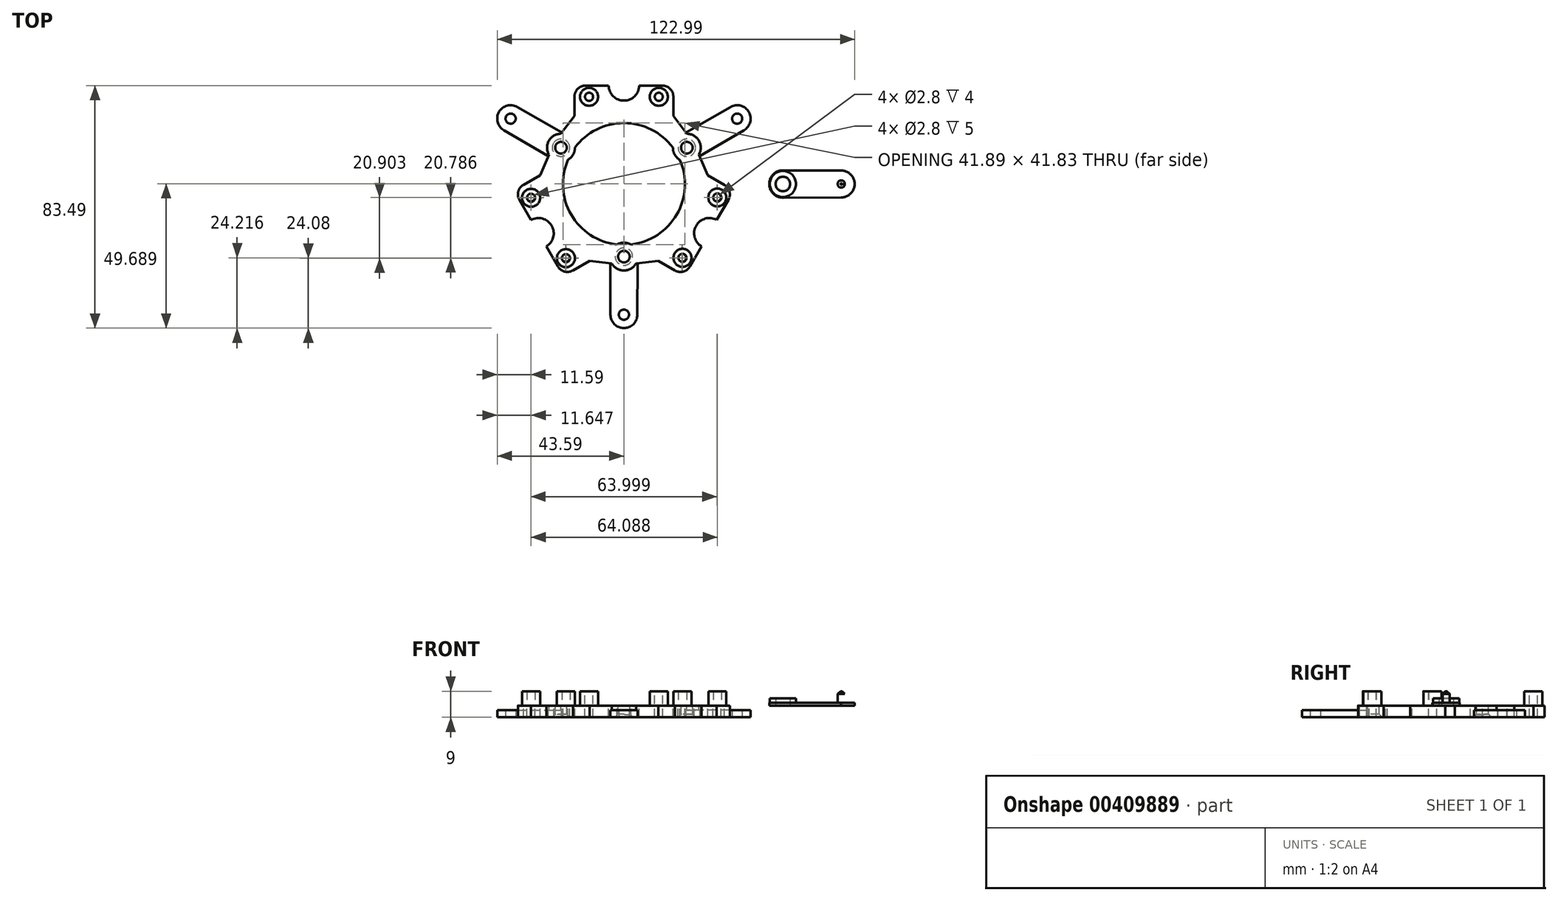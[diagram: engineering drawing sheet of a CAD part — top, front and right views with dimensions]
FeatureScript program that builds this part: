
annotation { "Feature Type Name" : "Feature", "Feature Type Description" : "" }
export const myFeature = defineFeature(function(context is Context, id is Id, definition is map)
    precondition{}
    {
        {
            var Q0;
            Q0=qCreatedBy(makeId("Front.planeOp"),FACE);
            var sketch = newSketch(context, id + "F0", { "sketchPlane" : qUnion([Q0])});
            skLineSegment(sketch, "E0", {"start": v(0, 0) * mm, "end": v(0, 50) * mm});
            skSolve(sketch);
        }
        {
            var Q0;
            Q0=qCreatedBy(makeId("Top.planeOp"),FACE);
            var sketch = newSketch(context, id + "F1", { "sketchPlane" : qUnion([Q0])});
            skCircle(sketch, "E1.cCircle", {"center": v(0, 0) * mm, "radius": 30.02 * mm, "construction": true});
            skLineSegment(sketch, "E1.0", {"start": v(-52, 30.02) * mm, "end": v(52, 30.02) * mm});
            skLineSegment(sketch, "E1.1", {"start": v(52, 30.02) * mm, "end": v(0, -60.04) * mm});
            skLineSegment(sketch, "E1.2", {"start": v(0, -60.04) * mm, "end": v(-52, 30.02) * mm});
            skPoint(sketch, "E1.0.midPoint", {"position": v(0, 30.02) * mm});
            skCircle(sketch, "E2", {"center": v(12, 30.02) * mm, "radius": 1.25 * mm});
            skCircle(sketch, "E3.MirrorC", {"center": v(-12, 30.02) * mm, "radius": 1.25 * mm});
            skCircle(sketch, "E4.1.0", {"center": v(-32, -4.62) * mm, "radius": 1.25 * mm});
            skCircle(sketch, "E4.1.1", {"center": v(-20, -25.4) * mm, "radius": 1.25 * mm});
            skCircle(sketch, "E4.2.0", {"center": v(20, -25.4) * mm, "radius": 1.25 * mm});
            skCircle(sketch, "E4.2.1", {"center": v(32, -4.62) * mm, "radius": 1.25 * mm});
            skSolve(sketch);
        }
        {
            var Q0;
            Q0=qCreatedBy(makeId("Top.planeOp"),FACE);
            var sketch = newSketch(context, id + "F2", { "sketchPlane" : qUnion([Q0])});
            skLineSegment(sketch, "E5", {"start": v(5.25, 33.87) * mm, "end": v(10.75, 33.87) * mm});
            skArc(sketch, "E6", {"start": v(16.85, 12.5) * mm, "mid": v(9.43, 18.74) * mm, "end": v(0, 20.98) * mm});
            skArc(sketch, "E7", {"start": v(0, 28.71) * mm, "mid": v(3.68, 30.22) * mm, "end": v(5.25, 33.87) * mm});
            skLineSegment(sketch, "E8", {"start": v(10.75, 33.87) * mm, "end": v(13.25, 33.87) * mm});
            skLineSegment(sketch, "E9", {"start": v(12, 33.87) * mm, "end": v(12, 30.02) * mm});
            skCircle(sketch, "E10", {"center": v(21.65, 12.5) * mm, "radius": 2 * mm});
            skArc(sketch, "E11", {"start": v(16.85, 12.5) * mm, "mid": v(25.04, 9.1) * mm, "end": v(21.65, 17.3) * mm});
            skArc(sketch, "E12", {"start": v(17, 30.02) * mm, "mid": v(15.94, 32.74) * mm, "end": v(13.25, 33.87) * mm});
            skLineSegment(sketch, "E13", {"start": v(17, 30.02) * mm, "end": v(17, 23.47) * mm});
            skLineSegment(sketch, "E14", {"start": v(17, 23.47) * mm, "end": v(21.65, 17.3) * mm});
            skLineSegment(sketch, "E15.MirrorCS", {"start": v(-10.75, 33.87) * mm, "end": v(-13.25, 33.87) * mm});
            skLineSegment(sketch, "E16.MirrorCS", {"start": v(-12, 33.87) * mm, "end": v(-12, 30.02) * mm});
            skLineSegment(sketch, "E17.MirrorCS", {"start": v(-17, 23.47) * mm, "end": v(-21.65, 17.3) * mm});
            skArc(sketch, "E18.MirrorCS", {"start": v(-16.85, 12.5) * mm, "mid": v(-25.04, 9.1) * mm, "end": v(-21.65, 17.3) * mm});
            skLineSegment(sketch, "E19.MirrorCS", {"start": v(-5.25, 33.87) * mm, "end": v(-10.75, 33.87) * mm});
            skLineSegment(sketch, "E20.MirrorCS", {"start": v(-17, 30.02) * mm, "end": v(-17, 23.47) * mm});
            skArc(sketch, "E21.MirrorCS", {"start": v(-17, 30.02) * mm, "mid": v(-15.94, 32.74) * mm, "end": v(-13.25, 33.87) * mm});
            skCircle(sketch, "E22.MirrorC", {"center": v(-21.65, 12.5) * mm, "radius": 2 * mm});
            skArc(sketch, "E23.MirrorCS", {"start": v(0, 28.71) * mm, "mid": v(-3.68, 30.22) * mm, "end": v(-5.25, 33.87) * mm});
            skArc(sketch, "E24.MirrorCS", {"start": v(-16.85, 12.5) * mm, "mid": v(-9.43, 18.74) * mm, "end": v(0, 20.98) * mm});
            skArc(sketch, "E25.1.0", {"start": v(-24.87, -14.36) * mm, "mid": v(-28, -11.92) * mm, "end": v(-31.96, -12.39) * mm});
            skLineSegment(sketch, "E25.1.1", {"start": v(-23.33, -27.33) * mm, "end": v(-20, -25.4) * mm});
            skArc(sketch, "E25.1.2", {"start": v(-19.25, 8.34) * mm, "mid": v(-20.4, 17.14) * mm, "end": v(-25.8, 10.1) * mm});
            skLineSegment(sketch, "E25.1.4", {"start": v(-31.96, -12.39) * mm, "end": v(-34.7, -7.63) * mm});
            skLineSegment(sketch, "E25.1.5", {"start": v(-35.33, -6.54) * mm, "end": v(-32, -4.62) * mm});
            skArc(sketch, "E25.1.6", {"start": v(-19.25, 8.34) * mm, "mid": v(-20.95, -1.2) * mm, "end": v(-18.17, -10.5) * mm});
            skArc(sketch, "E25.1.7", {"start": v(-34.5, -0.29) * mm, "mid": v(-36.32, -2.57) * mm, "end": v(-35.96, -5.46) * mm});
            skArc(sketch, "E25.1.8", {"start": v(-24.87, -14.36) * mm, "mid": v(-24.33, -18.3) * mm, "end": v(-26.7, -21.48) * mm});
            skCircle(sketch, "E25.1.9", {"center": v(0, -25) * mm, "radius": 2 * mm});
            skLineSegment(sketch, "E25.1.10", {"start": v(-28.83, 2.99) * mm, "end": v(-25.8, 10.1) * mm});
            skArc(sketch, "E25.1.11", {"start": v(-2.4, -20.84) * mm, "mid": v(-11.51, -17.54) * mm, "end": v(-18.17, -10.5) * mm});
            skArc(sketch, "E25.1.12", {"start": v(-17.5, -29.73) * mm, "mid": v(-20.38, -30.17) * mm, "end": v(-22.7, -28.41) * mm});
            skLineSegment(sketch, "E25.1.13", {"start": v(-34.5, -0.29) * mm, "end": v(-28.83, 2.99) * mm});
            skArc(sketch, "E25.1.14", {"start": v(-2.4, -20.84) * mm, "mid": v(4.64, -26.24) * mm, "end": v(-4.16, -27.4) * mm});
            skLineSegment(sketch, "E25.1.15", {"start": v(-26.7, -21.48) * mm, "end": v(-23.96, -26.24) * mm});
            skLineSegment(sketch, "E25.1.16", {"start": v(-11.83, -26.46) * mm, "end": v(-4.16, -27.4) * mm});
            skLineSegment(sketch, "E25.1.17", {"start": v(-17.5, -29.73) * mm, "end": v(-11.83, -26.46) * mm});
            skLineSegment(sketch, "E25.1.18", {"start": v(-34.7, -7.63) * mm, "end": v(-35.96, -5.46) * mm});
            skLineSegment(sketch, "E25.1.19", {"start": v(-23.96, -26.24) * mm, "end": v(-22.7, -28.41) * mm});
            skArc(sketch, "E25.2.0", {"start": v(24.87, -14.36) * mm, "mid": v(24.33, -18.3) * mm, "end": v(26.7, -21.48) * mm});
            skLineSegment(sketch, "E25.2.1", {"start": v(35.33, -6.54) * mm, "end": v(32, -4.62) * mm});
            skArc(sketch, "E25.2.2", {"start": v(2.4, -20.84) * mm, "mid": v(-4.64, -26.24) * mm, "end": v(4.16, -27.4) * mm});
            skCircle(sketch, "E25.2.3", {"center": v(0, -25) * mm, "radius": 2 * mm});
            skLineSegment(sketch, "E25.2.4", {"start": v(26.7, -21.48) * mm, "end": v(23.96, -26.24) * mm});
            skLineSegment(sketch, "E25.2.5", {"start": v(23.33, -27.33) * mm, "end": v(20, -25.4) * mm});
            skArc(sketch, "E25.2.6", {"start": v(2.4, -20.84) * mm, "mid": v(11.51, -17.54) * mm, "end": v(18.17, -10.5) * mm});
            skArc(sketch, "E25.2.7", {"start": v(17.5, -29.73) * mm, "mid": v(20.38, -30.17) * mm, "end": v(22.7, -28.41) * mm});
            skArc(sketch, "E25.2.8", {"start": v(24.87, -14.36) * mm, "mid": v(28, -11.92) * mm, "end": v(31.96, -12.39) * mm});
            skLineSegment(sketch, "E25.2.10", {"start": v(11.83, -26.46) * mm, "end": v(4.16, -27.4) * mm});
            skArc(sketch, "E25.2.11", {"start": v(19.25, 8.34) * mm, "mid": v(20.95, -1.2) * mm, "end": v(18.17, -10.5) * mm});
            skArc(sketch, "E25.2.12", {"start": v(34.5, -0.29) * mm, "mid": v(36.32, -2.57) * mm, "end": v(35.96, -5.46) * mm});
            skLineSegment(sketch, "E25.2.13", {"start": v(17.5, -29.73) * mm, "end": v(11.83, -26.46) * mm});
            skArc(sketch, "E25.2.14", {"start": v(19.25, 8.34) * mm, "mid": v(20.4, 17.14) * mm, "end": v(25.8, 10.1) * mm});
            skLineSegment(sketch, "E25.2.15", {"start": v(31.96, -12.39) * mm, "end": v(34.7, -7.63) * mm});
            skLineSegment(sketch, "E25.2.16", {"start": v(28.83, 2.99) * mm, "end": v(25.8, 10.1) * mm});
            skLineSegment(sketch, "E25.2.17", {"start": v(34.5, -0.29) * mm, "end": v(28.83, 2.99) * mm});
            skLineSegment(sketch, "E25.2.18", {"start": v(23.96, -26.24) * mm, "end": v(22.7, -28.41) * mm});
            skLineSegment(sketch, "E25.2.19", {"start": v(34.7, -7.63) * mm, "end": v(35.96, -5.46) * mm});
            skCircle(sketch, "E26", {"center": v(12, 30.02) * mm, "radius": 1.4 * mm});
            skCircle(sketch, "E27.MirrorC", {"center": v(-12, 30.02) * mm, "radius": 1.4 * mm});
            skCircle(sketch, "E28.1.0", {"center": v(-32, -4.62) * mm, "radius": 1.4 * mm});
            skCircle(sketch, "E28.1.1", {"center": v(-20, -25.4) * mm, "radius": 1.4 * mm});
            skCircle(sketch, "E28.2.0", {"center": v(20, -25.4) * mm, "radius": 1.4 * mm});
            skCircle(sketch, "E28.2.1", {"center": v(32, -4.62) * mm, "radius": 1.4 * mm});
            skSolve(sketch);
        }
        {
            var Q0;
            Q0=qSketchRegion(id+"F2",true);
            extrude(context, id + "F3", {"entities" : qUnion([Q0]), "oppositeDirection" : true, "depth" : 4 * mm});
        }
        {
            var Q0;
            Q0=makeQuery(id+"F3.opExtrude","CAP_FACE",FACE,{"disambiguationData":[OSD([sQuery(id+"F2.wireOp",EDGE,"E5"),sQuery(id+"F2.wireOp",EDGE,"E6"),sQuery(id+"F2.wireOp",EDGE,"OTH0FymN-yfsN-0UsN-41Kz-5CJosObtJ083"),sQuery(id+"F2.wireOp",EDGE,"3A02pTdK-AV8J-qCXS-i5Cg-76qnhJVGPjWh"),sQuery(id+"F2.wireOp",EDGE,"5Z3o6wOb-oYhe-xRQF-fwUz-g2kkQ9HctwZJ"),sQuery(id+"F2.wireOp",EDGE,"E7"),sQuery(id+"F2.wireOp",EDGE,"AUobkKVc-RQ03-aKL8-U0OO-zYTzcYtjvFHw"),sQuery(id+"F2.wireOp",EDGE,"E8"),sQuery(id+"F2.wireOp",EDGE,"624812f1-2ad6-4ab7-8a89-68286fdeb31e8.MirrorCS"),sQuery(id+"F2.wireOp",EDGE,"624812f1-2ad6-4ab7-8a89-68286fdeb31e9.MirrorCS"),sQuery(id+"F2.wireOp",EDGE,"624812f1-2ad6-4ab7-8a89-68286fdeb31e10.MirrorCS"),sQuery(id+"F2.wireOp",EDGE,"624812f1-2ad6-4ab7-8a89-68286fdeb31e11.MirrorCS"),sQuery(id+"F2.wireOp",EDGE,"624812f1-2ad6-4ab7-8a89-68286fdeb31e12.MirrorCS"),sQuery(id+"F2.wireOp",EDGE,"624812f1-2ad6-4ab7-8a89-68286fdeb31e14.MirrorCS"),sQuery(id+"F2.wireOp",EDGE,"624812f1-2ad6-4ab7-8a89-68286fdeb31e15.MirrorCS"),sQuery(id+"F2.wireOp",EDGE,"624812f1-2ad6-4ab7-8a89-68286fdeb31e16.MirrorCS"),sQuery(id+"F2.wireOp",EDGE,"36ff6b61-fbfb-4fdb-958a-ac3ee2e7cda7.1.1"),sQuery(id+"F2.wireOp",EDGE,"36ff6b61-fbfb-4fdb-958a-ac3ee2e7cda7.1.2"),sQuery(id+"F2.wireOp",EDGE,"36ff6b61-fbfb-4fdb-958a-ac3ee2e7cda7.1.3"),sQuery(id+"F2.wireOp",EDGE,"36ff6b61-fbfb-4fdb-958a-ac3ee2e7cda7.1.4"),sQuery(id+"F2.wireOp",EDGE,"36ff6b61-fbfb-4fdb-958a-ac3ee2e7cda7.1.5"),sQuery(id+"F2.wireOp",EDGE,"36ff6b61-fbfb-4fdb-958a-ac3ee2e7cda7.1.6"),sQuery(id+"F2.wireOp",EDGE,"36ff6b61-fbfb-4fdb-958a-ac3ee2e7cda7.1.7"),sQuery(id+"F2.wireOp",EDGE,"36ff6b61-fbfb-4fdb-958a-ac3ee2e7cda7.1.8"),sQuery(id+"F2.wireOp",EDGE,"36ff6b61-fbfb-4fdb-958a-ac3ee2e7cda7.1.9"),sQuery(id+"F2.wireOp",EDGE,"36ff6b61-fbfb-4fdb-958a-ac3ee2e7cda7.1.10"),sQuery(id+"F2.wireOp",EDGE,"36ff6b61-fbfb-4fdb-958a-ac3ee2e7cda7.1.11"),sQuery(id+"F2.wireOp",EDGE,"36ff6b61-fbfb-4fdb-958a-ac3ee2e7cda7.1.12"),sQuery(id+"F2.wireOp",EDGE,"36ff6b61-fbfb-4fdb-958a-ac3ee2e7cda7.1.15"),sQuery(id+"F2.wireOp",EDGE,"36ff6b61-fbfb-4fdb-958a-ac3ee2e7cda7.1.16"),sQuery(id+"F2.wireOp",EDGE,"36ff6b61-fbfb-4fdb-958a-ac3ee2e7cda7.1.17"),sQuery(id+"F2.wireOp",EDGE,"36ff6b61-fbfb-4fdb-958a-ac3ee2e7cda7.1.19"),sQuery(id+"F2.wireOp",EDGE,"36ff6b61-fbfb-4fdb-958a-ac3ee2e7cda7.2.1"),sQuery(id+"F2.wireOp",EDGE,"36ff6b61-fbfb-4fdb-958a-ac3ee2e7cda7.2.2"),sQuery(id+"F2.wireOp",EDGE,"36ff6b61-fbfb-4fdb-958a-ac3ee2e7cda7.2.3"),sQuery(id+"F2.wireOp",EDGE,"36ff6b61-fbfb-4fdb-958a-ac3ee2e7cda7.2.4"),sQuery(id+"F2.wireOp",EDGE,"36ff6b61-fbfb-4fdb-958a-ac3ee2e7cda7.2.5"),sQuery(id+"F2.wireOp",EDGE,"36ff6b61-fbfb-4fdb-958a-ac3ee2e7cda7.2.6"),sQuery(id+"F2.wireOp",EDGE,"36ff6b61-fbfb-4fdb-958a-ac3ee2e7cda7.2.7"),sQuery(id+"F2.wireOp",EDGE,"36ff6b61-fbfb-4fdb-958a-ac3ee2e7cda7.2.8"),sQuery(id+"F2.wireOp",EDGE,"36ff6b61-fbfb-4fdb-958a-ac3ee2e7cda7.2.9"),sQuery(id+"F2.wireOp",EDGE,"36ff6b61-fbfb-4fdb-958a-ac3ee2e7cda7.2.10"),sQuery(id+"F2.wireOp",EDGE,"36ff6b61-fbfb-4fdb-958a-ac3ee2e7cda7.2.11"),sQuery(id+"F2.wireOp",EDGE,"36ff6b61-fbfb-4fdb-958a-ac3ee2e7cda7.2.12"),sQuery(id+"F2.wireOp",EDGE,"36ff6b61-fbfb-4fdb-958a-ac3ee2e7cda7.2.15"),sQuery(id+"F2.wireOp",EDGE,"36ff6b61-fbfb-4fdb-958a-ac3ee2e7cda7.2.16"),sQuery(id+"F2.wireOp",EDGE,"36ff6b61-fbfb-4fdb-958a-ac3ee2e7cda7.2.17"),sQuery(id+"F2.wireOp",EDGE,"36ff6b61-fbfb-4fdb-958a-ac3ee2e7cda7.2.19")])],"isStart":true});
            var sketch = newSketch(context, id + "F4", { "sketchPlane" : qUnion([Q0])});
            skCircle(sketch, "E29", {"center": v(12, 30.02) * mm, "radius": 1.4 * mm});
            skCircle(sketch, "E30", {"center": v(12, 30.02) * mm, "radius": 3.1 * mm});
            skCircle(sketch, "E31.MirrorC", {"center": v(-12, 30.02) * mm, "radius": 1.4 * mm});
            skCircle(sketch, "E32.MirrorC", {"center": v(-12, 30.02) * mm, "radius": 3.1 * mm});
            skCircle(sketch, "E33.1.0", {"center": v(-19.94, -25.54) * mm, "radius": 3.1 * mm});
            skCircle(sketch, "E33.1.1", {"center": v(-31.94, -4.75) * mm, "radius": 3.1 * mm});
            skCircle(sketch, "E33.1.2", {"center": v(-19.94, -25.54) * mm, "radius": 1.4 * mm});
            skCircle(sketch, "E33.1.3", {"center": v(-31.94, -4.75) * mm, "radius": 1.4 * mm});
            skCircle(sketch, "E33.2.0", {"center": v(32.15, -4.64) * mm, "radius": 3.1 * mm});
            skCircle(sketch, "E33.2.1", {"center": v(20.15, -25.42) * mm, "radius": 3.1 * mm});
            skCircle(sketch, "E33.2.2", {"center": v(32.15, -4.64) * mm, "radius": 1.4 * mm});
            skCircle(sketch, "E33.2.3", {"center": v(20.15, -25.42) * mm, "radius": 1.4 * mm});
            skPoint(sketch, "E33.center", {"position": v(0.07, -0.05) * mm});
            skSolve(sketch);
        }
        {
            var Q0;
            Q0=qSketchRegion(id+"F4",true);
            extrude(context, id + "F5", {"entities" : qUnion([Q0]), "operationType" : NewBodyOperationType.ADD, "depth" : 5 * mm});
        }
        {
            var Q0;
            Q0=qCreatedBy(makeId("Top.planeOp"),FACE);
            cPlane(context, id + "F6", {"entities" : qUnion([Q0]), "cplaneType" : CPlaneType.OFFSET, "offset" : 2 * mm, "oppositeDirection" : true, "width" : 150 * mm, "height" : 150 * mm});
        }
        {
            var Q0;
            Q0=makeQuery(id+"F3.opExtrude","CAP_FACE",FACE,{"disambiguationData":[OSD([sQuery(id+"F2.wireOp",EDGE,"E5"),sQuery(id+"F2.wireOp",EDGE,"E6"),sQuery(id+"F2.wireOp",EDGE,"E7"),sQuery(id+"F2.wireOp",EDGE,"E8"),sQuery(id+"F2.wireOp",EDGE,"E10"),sQuery(id+"F2.wireOp",EDGE,"E11"),sQuery(id+"F2.wireOp",EDGE,"E12"),sQuery(id+"F2.wireOp",EDGE,"E13"),sQuery(id+"F2.wireOp",EDGE,"E14"),sQuery(id+"F2.wireOp",EDGE,"E15.MirrorCS"),sQuery(id+"F2.wireOp",EDGE,"E17.MirrorCS"),sQuery(id+"F2.wireOp",EDGE,"E18.MirrorCS"),sQuery(id+"F2.wireOp",EDGE,"E19.MirrorCS"),sQuery(id+"F2.wireOp",EDGE,"E20.MirrorCS"),sQuery(id+"F2.wireOp",EDGE,"E21.MirrorCS"),sQuery(id+"F2.wireOp",EDGE,"E22.MirrorC"),sQuery(id+"F2.wireOp",EDGE,"E23.MirrorCS"),sQuery(id+"F2.wireOp",EDGE,"E24.MirrorCS"),sQuery(id+"F2.wireOp",EDGE,"E25.1.0"),sQuery(id+"F2.wireOp",EDGE,"E25.1.2"),sQuery(id+"F2.wireOp",EDGE,"E22.MirrorC"),sQuery(id+"F2.wireOp",EDGE,"E25.1.4"),sQuery(id+"F2.wireOp",EDGE,"E25.1.6"),sQuery(id+"F2.wireOp",EDGE,"E25.1.7"),sQuery(id+"F2.wireOp",EDGE,"E25.1.8"),sQuery(id+"F2.wireOp",EDGE,"E25.1.9"),sQuery(id+"F2.wireOp",EDGE,"E25.1.10"),sQuery(id+"F2.wireOp",EDGE,"E25.1.11"),sQuery(id+"F2.wireOp",EDGE,"E25.1.12"),sQuery(id+"F2.wireOp",EDGE,"E25.1.13"),sQuery(id+"F2.wireOp",EDGE,"E25.1.14"),sQuery(id+"F2.wireOp",EDGE,"E25.1.15"),sQuery(id+"F2.wireOp",EDGE,"E25.1.16"),sQuery(id+"F2.wireOp",EDGE,"E25.1.17"),sQuery(id+"F2.wireOp",EDGE,"E25.1.18"),sQuery(id+"F2.wireOp",EDGE,"E25.1.19"),sQuery(id+"F2.wireOp",EDGE,"E25.2.0"),sQuery(id+"F2.wireOp",EDGE,"E25.2.2"),sQuery(id+"F2.wireOp",EDGE,"E25.2.3"),sQuery(id+"F2.wireOp",EDGE,"E25.2.4"),sQuery(id+"F2.wireOp",EDGE,"E25.2.6"),sQuery(id+"F2.wireOp",EDGE,"E25.2.7"),sQuery(id+"F2.wireOp",EDGE,"E25.2.8"),sQuery(id+"F2.wireOp",EDGE,"E10"),sQuery(id+"F2.wireOp",EDGE,"E25.2.10"),sQuery(id+"F2.wireOp",EDGE,"E25.2.11"),sQuery(id+"F2.wireOp",EDGE,"E25.2.12"),sQuery(id+"F2.wireOp",EDGE,"E25.2.13"),sQuery(id+"F2.wireOp",EDGE,"E25.2.14"),sQuery(id+"F2.wireOp",EDGE,"E25.2.15"),sQuery(id+"F2.wireOp",EDGE,"E25.2.16"),sQuery(id+"F2.wireOp",EDGE,"E25.2.17"),sQuery(id+"F2.wireOp",EDGE,"E25.2.18"),sQuery(id+"F2.wireOp",EDGE,"E25.2.19")])],"isStart":false});
            var sketch = newSketch(context, id + "F7", { "sketchPlane" : qUnion([Q0])});
            skLineSegment(sketch, "E34", {"start": v(0, 0) * mm, "end": v(21.65, -12.5) * mm});
            skCircle(sketch, "E35", {"center": v(21.65, -12.5) * mm, "radius": 4.7 * mm});
            skLineSegment(sketch, "E36", {"start": v(21.65, -12.5) * mm, "end": v(19.3, -16.57) * mm});
            skLineSegment(sketch, "E37", {"start": v(21.65, -12.5) * mm, "end": v(37.45, -21.62) * mm});
            skArc(sketch, "E38", {"start": v(37.45, -21.62) * mm, "mid": v(38.1, -24.01) * mm, "end": v(40.49, -23.37) * mm});
            skArc(sketch, "E39", {"start": v(36.66, -26.5) * mm, "mid": v(40.17, -26.96) * mm, "end": v(42.98, -24.8) * mm});
            skLineSegment(sketch, "E40", {"start": v(40.49, -23.37) * mm, "end": v(42.98, -24.8) * mm});
            skArc(sketch, "E41.MirrorCS", {"start": v(37.45, -21.62) * mm, "mid": v(39.84, -20.98) * mm, "end": v(40.49, -23.37) * mm});
            skCircle(sketch, "E42", {"center": v(21.65, -12.5) * mm, "radius": 2.5 * mm});
            skLineSegment(sketch, "E43", {"start": v(36.66, -26.5) * mm, "end": v(19.3, -16.57) * mm});
            skLineSegment(sketch, "E44.MirrorCS", {"start": v(41.29, -18.5) * mm, "end": v(24, -8.43) * mm});
            skArc(sketch, "E45.MirrorCS", {"start": v(41.29, -18.5) * mm, "mid": v(43.44, -21.3) * mm, "end": v(42.98, -24.8) * mm});
            skSolve(sketch);
        }
        {
            var Q0;
            Q0=qSketchRegion(id+"F7",true);
            extrude(context, id + "F8", {"entities" : qUnion([Q0]), "oppositeDirection" : true, "depth" : 2.5 * mm});
        }
        {
            var Q0;
            Q0=makeQuery(id+"F8.opExtrude","SWEPT_BODY",BODY,{"disambiguationData":[OSD([sQuery(id+"F7.wireOp",EDGE,"E35"),sQuery(id+"F7.wireOp",EDGE,"E38"),sQuery(id+"F7.wireOp",EDGE,"E39"),sQuery(id+"F7.wireOp",EDGE,"9kqUA9Jo-edwP-NO00-sSji-nR2odCKgbMeb"),sQuery(id+"F7.wireOp",EDGE,"GDexJB8U-NTdd-inDH-WQeI-0l2QnxEohQ9h"),sQuery(id+"F7.wireOp",EDGE,"JeVKlujZ-zA6a-IIGW-YSz6-gVSeSdLv3vhB"),sQuery(id+"F7.wireOp",EDGE,"MW1JaytO-XEjq-5YeB-MR8k-oZC2Z9Jpgj3d"),sQuery(id+"F7.wireOp",EDGE,"Y6P3fMeu-8VPu-QNSC-VJmo-vZOKqAch7LHx"),sQuery(id+"F7.wireOp",EDGE,"4fPfChJr-W4YN-7BBy-D4l4-nojVqKYKC0ln"),sQuery(id+"F7.wireOp",EDGE,"2de3917a-e362-44b2-9ee0-3e3d1b5f62ab.trimOffspring"),sQuery(id+"F7.wireOp",EDGE,"E40"),sQuery(id+"F7.wireOp",EDGE,"7557a1f4-8a86-41d2-b121-450dcfc2fc1b0.MirrorCS"),sQuery(id+"F7.wireOp",EDGE,"d8fe862a-e72c-42c7-bef4-22f0e19987d60.MirrorCS"),sQuery(id+"F7.wireOp",EDGE,"e1d4639a-9bbe-4f0b-9f0e-1e47ea0f83f50.MirrorCS"),sQuery(id+"F7.wireOp",EDGE,"bf0646c6-655b-4980-9d40-1a8a652c793b0.MirrorCS"),sQuery(id+"F7.wireOp",EDGE,"28871922-5b9a-4380-b66f-36384049dd340.MirrorCS"),sQuery(id+"F7.wireOp",EDGE,"f77bd1d0-2b69-4607-9877-85ea826859d50.MirrorCS"),sQuery(id+"F7.wireOp",EDGE,"4006c2c9-1f6f-453f-8150-a3eb66e0c37a0.MirrorCS"),sQuery(id+"F7.wireOp",EDGE,"1c3aa9cd-c4e5-4692-9f40-bda29d6e96f20.MirrorCS"),sQuery(id+"F7.wireOp",EDGE,"E40"),sQuery(id+"F7.wireOp",EDGE,"E41.MirrorCS"),sQuery(id+"F7.wireOp",EDGE,"E42")])]});
            var Q1;
            Q1=sQuery(id+"F0.wireOp",EDGE,"E0");
            circularPattern(context, id + "F9", {"operationType" : NewBodyOperationType.ADD, "entities" : qUnion([Q0]), "axis" : qUnion([Q1]), "angle" : 360 * degree, "instanceCount" : 3, "equalSpace" : true});
        }
        {
            var Q0;
            Q0=makeQuery(id+"F3.opExtrude","CAP_EDGE",EDGE,{"disambiguationData":[OSD([sQuery(id+"F2.wireOp",EDGE,"E22.MirrorC")])],"isStart":false});
            var Q1;
            Q1=makeQuery(id+"F3.opExtrude","CAP_EDGE",EDGE,{"disambiguationData":[OSD([sQuery(id+"F2.wireOp",EDGE,"E10")])],"isStart":false});
            var Q2;
            Q2=makeQuery(id+"F3.opExtrude","CAP_EDGE",EDGE,{"disambiguationData":[OSD([sQuery(id+"F2.wireOp",EDGE,"E25.1.9")])],"isStart":false});
            chamfer(context, id + "F10", {"entities" : qUnion([Q0, Q1, Q2]), "width" : 1 * mm, "tangentPropagation" : true});
        }
        {
            var Q0;
            Q0=qCreatedBy(makeId("Top.planeOp"),FACE);
            var sketch = newSketch(context, id + "F11", { "sketchPlane" : qUnion([Q0])});
            skCircle(sketch, "E46", {"center": v(54.7, 0) * mm, "radius": 4.7 * mm});
            skLineSegment(sketch, "E47", {"start": v(54.7, 0) * mm, "end": v(54.7, -4.7) * mm});
            skLineSegment(sketch, "E48", {"start": v(54.7, 0) * mm, "end": v(73.53, 0) * mm});
            skArc(sketch, "E49", {"start": v(73.53, 0) * mm, "mid": v(74.78, -1.25) * mm, "end": v(76.03, 0) * mm});
            skArc(sketch, "E50", {"start": v(74.74, -4.62) * mm, "mid": v(78.04, -3.28) * mm, "end": v(79.4, 0) * mm});
            skLineSegment(sketch, "E51", {"start": v(76.03, 0) * mm, "end": v(79.4, 0) * mm});
            skArc(sketch, "E52.MirrorCS", {"start": v(73.53, 0) * mm, "mid": v(74.78, 1.25) * mm, "end": v(76.03, 0) * mm});
            skCircle(sketch, "E53", {"center": v(54.7, 0) * mm, "radius": 2.5 * mm});
            skLineSegment(sketch, "E54", {"start": v(74.74, -4.62) * mm, "end": v(54.7, -4.7) * mm});
            skLineSegment(sketch, "E55.MirrorCS", {"start": v(74.74, 4.63) * mm, "end": v(54.7, 4.7) * mm});
            skArc(sketch, "E56.MirrorCS", {"start": v(74.74, 4.63) * mm, "mid": v(78.04, 3.28) * mm, "end": v(79.4, 0) * mm});
            skSolve(sketch);
        }
        {
            var Q0;
            Q0=qSketchRegion(id+"F11",true);
            extrude(context, id + "F12", {"entities" : qUnion([Q0]), "depth" : 1 * mm});
        }
        {
            var Q0;
            Q0=makeQuery(id+"F12.opExtrude","CAP_FACE",FACE,{"disambiguationData":[OSD([sQuery(id+"F11.wireOp",EDGE,"E46"),sQuery(id+"F11.wireOp",EDGE,"E49"),sQuery(id+"F11.wireOp",EDGE,"E50"),sQuery(id+"F11.wireOp",EDGE,"E51"),sQuery(id+"F11.wireOp",EDGE,"E51"),sQuery(id+"F11.wireOp",EDGE,"E52.MirrorCS"),sQuery(id+"F11.wireOp",EDGE,"E53"),sQuery(id+"F11.wireOp",EDGE,"E54"),sQuery(id+"F11.wireOp",EDGE,"E55.MirrorCS"),sQuery(id+"F11.wireOp",EDGE,"E56.MirrorCS")])],"isStart":true});
            var sketch = newSketch(context, id + "F13", { "sketchPlane" : qUnion([Q0])});
            skCircle(sketch, "E57", {"center": v(54.7, 0) * mm, "radius": 2.5 * mm});
            skCircle(sketch, "E58", {"center": v(54.7, 0) * mm, "radius": 4.5 * mm});
            skSolve(sketch);
        }
        {
            var Q0;
            Q0=qSketchRegion(id+"F13",true);
            extrude(context, id + "F14", {"entities" : qUnion([Q0]), "operationType" : NewBodyOperationType.ADD, "oppositeDirection" : true, "depth" : 2.5 * mm});
        }
        {
            var Q0;
            Q0=makeQuery(id+"F12.opExtrude","CAP_FACE",FACE,{"disambiguationData":[OSD([sQuery(id+"F11.wireOp",EDGE,"E46"),sQuery(id+"F11.wireOp",EDGE,"E49"),sQuery(id+"F11.wireOp",EDGE,"E50"),sQuery(id+"F11.wireOp",EDGE,"E51"),sQuery(id+"F11.wireOp",EDGE,"E51"),sQuery(id+"F11.wireOp",EDGE,"E52.MirrorCS"),sQuery(id+"F11.wireOp",EDGE,"E53"),sQuery(id+"F11.wireOp",EDGE,"E54"),sQuery(id+"F11.wireOp",EDGE,"E55.MirrorCS"),sQuery(id+"F11.wireOp",EDGE,"E56.MirrorCS")])],"isStart":true});
            var sketch = newSketch(context, id + "F15", { "sketchPlane" : qUnion([Q0])});
            skCircle(sketch, "E59", {"center": v(74.78, 0) * mm, "radius": 1.25 * mm});
            skSolve(sketch);
        }
        {
            var Q0;
            Q0=qSketchRegion(id+"F15",true);
            extrude(context, id + "F16", {"entities" : qUnion([Q0]), "operationType" : NewBodyOperationType.ADD, "oppositeDirection" : true, "depth" : 5 * mm});
        }
        {
            var Q0;
            Q0=makeQuery(id+"F16.opExtrude","CAP_EDGE",EDGE,{"disambiguationData":[OSD([sQuery(id+"F15.wireOp",EDGE,"E59")])],"isStart":false});
            chamfer(context, id + "F17", {"entities" : qUnion([Q0]), "width" : 1 * mm, "tangentPropagation" : true});
        }
    });
